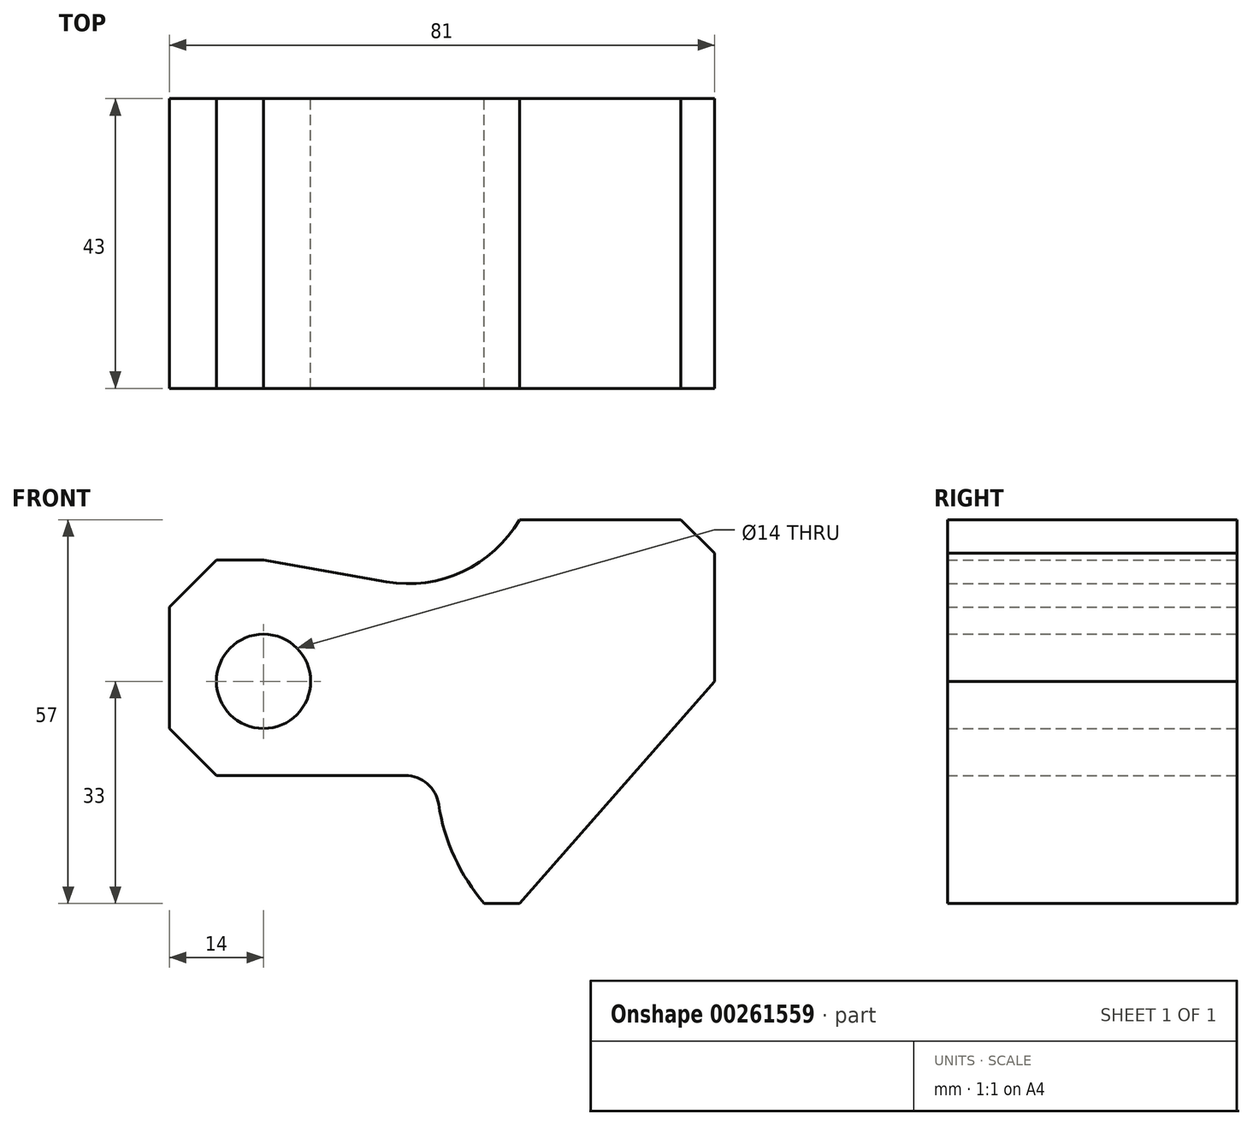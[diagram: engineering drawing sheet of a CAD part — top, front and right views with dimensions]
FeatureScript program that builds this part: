
annotation { "Feature Type Name" : "Feature", "Feature Type Description" : "" }
export const myFeature = defineFeature(function(context is Context, id is Id, definition is map)
    precondition{}
    {
        {
            var Q0;
            Q0=qCreatedBy(makeId("Front.planeOp"),FACE);
            var sketch = newSketch(context, id + "F0", { "sketchPlane" : qUnion([Q0])});
            skCircle(sketch, "E0", {"center": v(0, 0) * mm, "radius": 7 * mm});
            skLineSegment(sketch, "E1", {"start": v(0, 0) * mm, "end": v(-14, 0) * mm, "construction": true});
            skLineSegment(sketch, "E2", {"start": v(0, 0) * mm, "end": v(0, -14) * mm, "construction": true});
            skLineSegment(sketch, "E3", {"start": v(-14, -7) * mm, "end": v(-14, 11) * mm});
            skPoint(sketch, "E3.startSnap0", {"position": v(0, -7) * mm});
            skLineSegment(sketch, "E4", {"start": v(-14, -7) * mm, "end": v(-7, -14) * mm});
            skLineSegment(sketch, "E5", {"start": v(0, -14) * mm, "end": v(-7, -14) * mm});
            skPoint(sketch, "E6.start.orphan", {"position": v(-14, -14) * mm});
            skLineSegment(sketch, "E7", {"start": v(-14, 11) * mm, "end": v(-7, 18) * mm});
            skPoint(sketch, "E8.orphan", {"position": v(0, 25) * mm});
            skLineSegment(sketch, "E9", {"start": v(-7, 18) * mm, "end": v(0, 18) * mm});
            skLineSegment(sketch, "E10", {"start": v(-7, -14) * mm, "end": v(21.07, -14) * mm});
            skPoint(sketch, "E10.endSnap0", {"position": v(-3.5, -14) * mm});
            skLineSegment(sketch, "E11", {"start": v(0, 0) * mm, "end": v(7, 0) * mm});
            skPoint(sketch, "E12", {"position": v(21.07, -14) * mm});
            skPoint(sketch, "E13", {"position": v(67, 0) * mm});
            skLineSegment(sketch, "E14", {"start": v(67, 0) * mm, "end": v(67, 19) * mm});
            skLineSegment(sketch, "E15", {"start": v(67, 19) * mm, "end": v(62, 24) * mm});
            skLineSegment(sketch, "E16", {"start": v(62, 24) * mm, "end": v(38, 24) * mm});
            skArc(sketch, "E17", {"start": v(18.24, 14.78) * mm, "mid": v(29.57, 16.28) * mm, "end": v(38, 24) * mm});
            skLineSegment(sketch, "E18", {"start": v(0, 18) * mm, "end": v(18.24, 14.78) * mm});
            skLineSegment(sketch, "E19", {"start": v(67, 0) * mm, "end": v(67, -33) * mm, "construction": true});
            skLineSegment(sketch, "E20", {"start": v(67, -33) * mm, "end": v(38, -33) * mm, "construction": true});
            skLineSegment(sketch, "E21", {"start": v(67, 0) * mm, "end": v(38, -33) * mm});
            skLineSegment(sketch, "E22", {"start": v(54.7, -14) * mm, "end": v(54.7, -33) * mm, "construction": true});
            skArc(sketch, "E23", {"start": v(26.01, -18.26) * mm, "mid": v(24.33, -15.21) * mm, "end": v(21.07, -14) * mm});
            skLineSegment(sketch, "E24", {"start": v(38, -33) * mm, "end": v(32.79, -33) * mm});
            skArc(sketch, "E25", {"start": v(26.01, -18.26) * mm, "mid": v(28.35, -26.12) * mm, "end": v(32.79, -33) * mm});
            skSolve(sketch);
        }
        {
            var Q0;
            Q0=makeQuery(id+"F0.imprint","IMPRINT",FACE,{"disambiguationData":[TD([[makeQuery(id+"F0.imprint","IMPRINT",EDGE,{"derivedFrom":sQuery(id+"F0.wireOp",EDGE,"E0")}),-1.0]])]});
            extrude(context, id + "F1", {"entities" : qUnion([Q0]), "depth" : 43 * mm});
        }
    });
